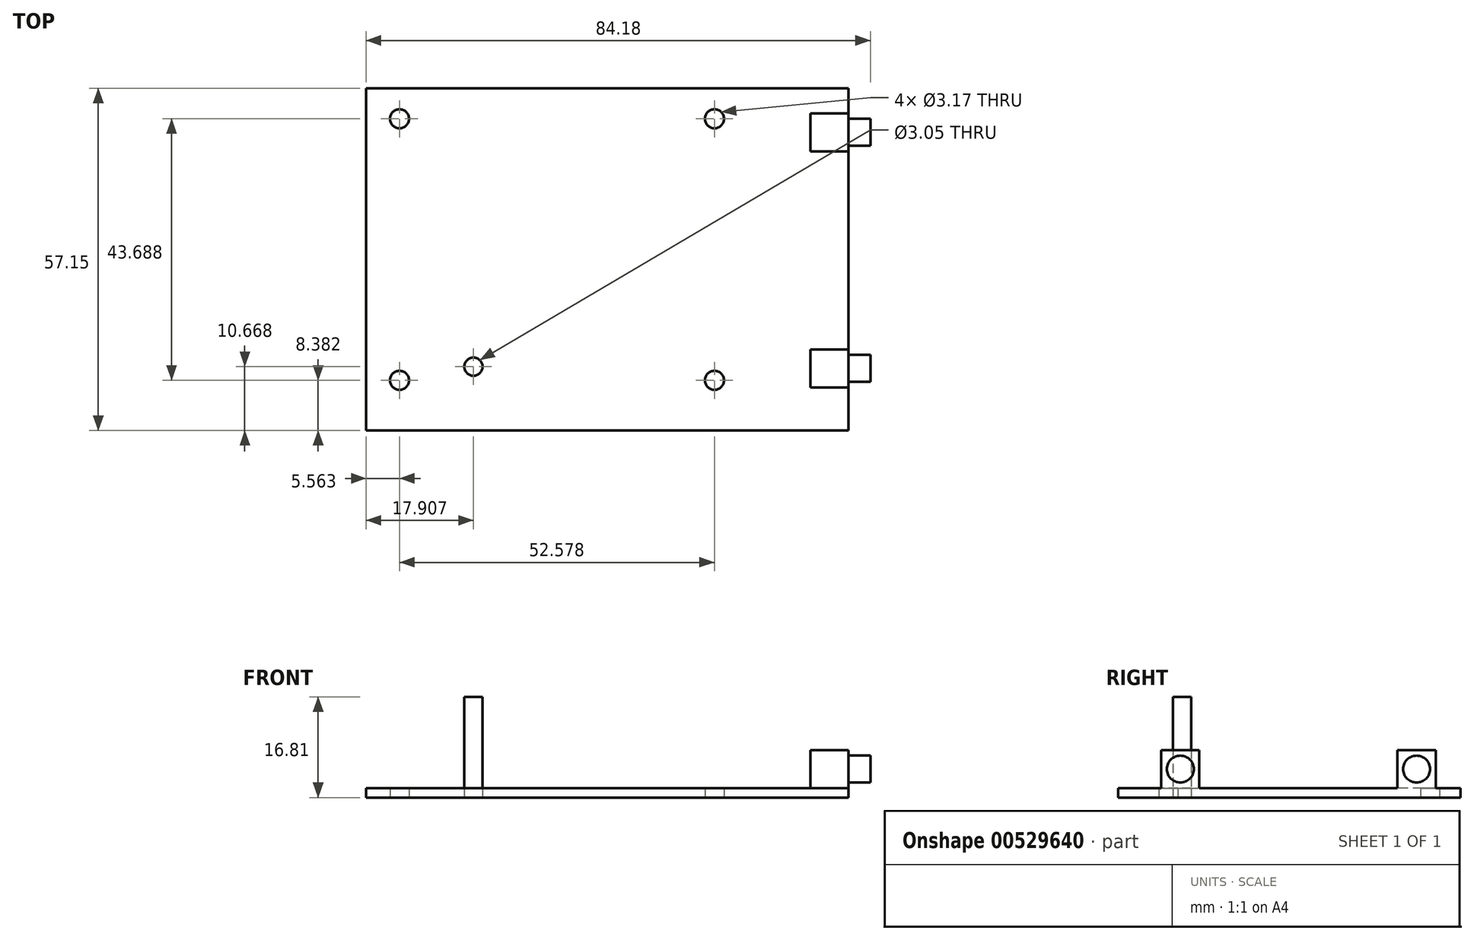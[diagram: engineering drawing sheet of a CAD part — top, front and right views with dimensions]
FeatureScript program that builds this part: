
annotation { "Feature Type Name" : "Feature", "Feature Type Description" : "" }
export const myFeature = defineFeature(function(context is Context, id is Id, definition is map)
    precondition{}
    {
        {
            var Q0;
            Q0=qCreatedBy(makeId("Top.planeOp"),FACE);
            var sketch = newSketch(context, id + "F0", { "sketchPlane" : qUnion([Q0])});
            skLineSegment(sketch, "E0.bottom", {"start": v(0, 0) * mm, "end": v(80.52, 0) * mm});
            skLineSegment(sketch, "E0.top", {"start": v(0, 57.15) * mm, "end": v(80.52, 57.15) * mm});
            skLineSegment(sketch, "E0.left", {"start": v(0, 0) * mm, "end": v(0, 57.15) * mm});
            skLineSegment(sketch, "E0.right", {"start": v(80.52, 0) * mm, "end": v(80.52, 57.15) * mm});
            skCircle(sketch, "E1", {"center": v(5.56, 8.38) * mm, "radius": 1.59 * mm});
            skCircle(sketch, "E2", {"center": v(58.14, 8.38) * mm, "radius": 1.59 * mm});
            skCircle(sketch, "E3", {"center": v(5.56, 52.07) * mm, "radius": 1.59 * mm});
            skCircle(sketch, "E4", {"center": v(58.14, 52.07) * mm, "radius": 1.59 * mm});
            skLineSegment(sketch, "E5.bottom", {"start": v(80.52, 8.05) * mm, "end": v(84.07, 8.05) * mm});
            skLineSegment(sketch, "E5.top", {"start": v(80.52, 12.62) * mm, "end": v(84.07, 12.62) * mm});
            skLineSegment(sketch, "E5.left", {"start": v(80.52, 8.05) * mm, "end": v(80.52, 12.62) * mm});
            skLineSegment(sketch, "E5.right", {"start": v(84.07, 8.05) * mm, "end": v(84.07, 12.62) * mm});
            skLineSegment(sketch, "E6.bottom", {"start": v(80.52, 47.55) * mm, "end": v(84.07, 47.55) * mm});
            skLineSegment(sketch, "E6.top", {"start": v(80.52, 52.12) * mm, "end": v(84.07, 52.12) * mm});
            skLineSegment(sketch, "E6.left", {"start": v(80.52, 47.55) * mm, "end": v(80.52, 52.12) * mm});
            skLineSegment(sketch, "E6.right", {"start": v(84.07, 47.55) * mm, "end": v(84.07, 52.12) * mm});
            skCircle(sketch, "E7", {"center": v(17.9, 10.67) * mm, "radius": 1.52 * mm});
            skSolve(sketch);
        }
        {
            var Q0;
            {var subQ4=sQuery(id+"F0.wireOp",EDGE,"E0.bottom");Q0=makeQuery(id+"F0.imprint","IMPRINT",FACE,{"disambiguationData":[TD([[makeQuery(id+"F0.imprint","IMPRINT",EDGE,{"derivedFrom":subQ4}),1.0]])]});}
            extrude(context, id + "F1", {"entities" : qUnion([Q0]), "depth" : 1.57 * mm, "offsetDistance" : 25.4 * mm});
        }
        {
            var Q0;
            Q0=makeQuery(id+"F1.opExtrude","CAP_FACE",FACE,{"disambiguationData":[OSD([sQuery(id+"F0.wireOp",EDGE,"E0.bottom"),sQuery(id+"F0.wireOp",EDGE,"E0.top"),sQuery(id+"F0.wireOp",EDGE,"E0.left"),sQuery(id+"F0.wireOp",EDGE,"E0.right"),sQuery(id+"F0.wireOp",EDGE,"E1"),sQuery(id+"F0.wireOp",EDGE,"E2"),sQuery(id+"F0.wireOp",EDGE,"E3"),sQuery(id+"F0.wireOp",EDGE,"E4"),sQuery(id+"F0.wireOp",EDGE,"E5.left"),sQuery(id+"F0.wireOp",EDGE,"E6.left"),sQuery(id+"F0.wireOp",EDGE,"E7")])],"isStart":false});
            var sketch = newSketch(context, id + "F2", { "sketchPlane" : qUnion([Q0])});
            skLineSegment(sketch, "E8.bottom", {"start": v(80.52, 7.2) * mm, "end": v(74.17, 7.2) * mm});
            skLineSegment(sketch, "E8.top", {"start": v(80.52, 13.55) * mm, "end": v(74.17, 13.55) * mm});
            skLineSegment(sketch, "E8.left", {"start": v(80.52, 7.2) * mm, "end": v(80.52, 13.55) * mm});
            skLineSegment(sketch, "E8.right", {"start": v(74.17, 7.2) * mm, "end": v(74.17, 13.55) * mm});
            skLineSegment(sketch, "E9", {"start": v(0, 28.58) * mm, "end": v(80.52, 28.58) * mm, "construction": true});
            skLineSegment(sketch, "E10.bottom", {"start": v(80.52, 52.99) * mm, "end": v(74.17, 52.99) * mm});
            skLineSegment(sketch, "E10.top", {"start": v(80.52, 46.64) * mm, "end": v(74.17, 46.64) * mm});
            skLineSegment(sketch, "E10.left", {"start": v(80.52, 52.99) * mm, "end": v(80.52, 46.64) * mm});
            skLineSegment(sketch, "E10.right", {"start": v(74.17, 52.99) * mm, "end": v(74.17, 46.64) * mm});
            skSolve(sketch);
        }
        {
            var Q0;
            Q0 = qSketchRegion(id + "F2", true);
            extrude(context, id + "F3", {"entities" : qUnion([Q0]), "operationType" : NewBodyOperationType.ADD, "depth" : 6.35 * mm, "offsetDistance" : 25.4 * mm});
        }
        {
            var Q0;
            Q0=makeQuery(id+"F3.boolean.opBoolean","MERGE",FACE,{"derivedFrom":[makeQuery(id+"F1.opExtrude","SWEPT_FACE",FACE,{"disambiguationData":[OSD([sQuery(id+"F0.wireOp",EDGE,"E0.right"),sQuery(id+"F0.wireOp",EDGE,"E5.left"),sQuery(id+"F0.wireOp",EDGE,"E6.left")])]}),makeQuery(id+"F3.opExtrude","SWEPT_FACE",FACE,{"disambiguationData":[OSD([sQuery(id+"F2.wireOp",EDGE,"E8.left")])]})]});
            var sketch = newSketch(context, id + "F4", { "sketchPlane" : qUnion([Q0])});
            skCircle(sketch, "E11", {"center": v(10.37, 4.75) * mm, "radius": 2.25 * mm});
            skPoint(sketch, "E11.centerSnap0", {"position": v(10.37, 7.92) * mm});
            skPoint(sketch, "E11.centerSnap1", {"position": v(13.55, 4.75) * mm});
            skCircle(sketch, "E12", {"center": v(49.81, 4.75) * mm, "radius": 2.25 * mm});
            skPoint(sketch, "E12.centerSnap0", {"position": v(49.81, 7.92) * mm});
            skPoint(sketch, "E12.centerSnap1", {"position": v(52.99, 4.75) * mm});
            skSolve(sketch);
        }
        {
            var Q0;
            Q0 = qSketchRegion(id + "F4", true);
            extrude(context, id + "F5", {"entities" : qUnion([Q0]), "operationType" : NewBodyOperationType.ADD, "depth" : 3.66 * mm, "offsetDistance" : 25.4 * mm});
        }
        {
            var Q0;
            Q0=makeQuery(id+"F2.imprint","IMPRINT",FACE,{"disambiguationData":[TD([[makeQuery(id+"F2.imprint","IMPRINT",EDGE,{"derivedFrom":makeQuery(id+"F1.opExtrude","CAP_EDGE",EDGE,{"disambiguationData":[OSD([sQuery(id+"F0.wireOp",EDGE,"E7")])],"isStart":false})}),1.0]])]});
            extrude(context, id + "F6", {"entities" : qUnion([Q0]), "depth" : 15.24 * mm, "offsetDistance" : 25.4 * mm});
        }
    });
